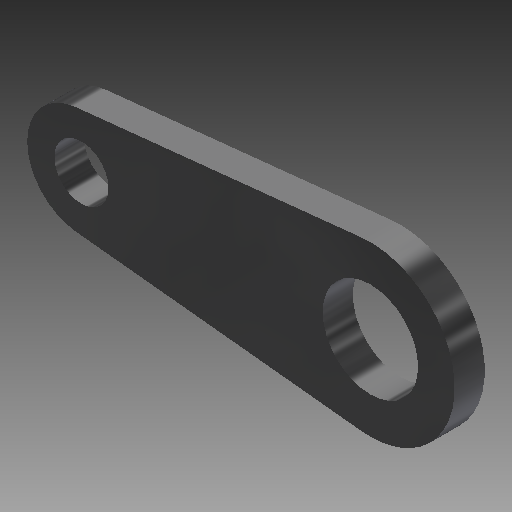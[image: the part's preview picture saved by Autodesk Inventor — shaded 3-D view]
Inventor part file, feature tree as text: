
AUTODESK INVENTOR PART (.ipt)
format: ipt  version: 2019 (Build 230136000, 136)  size: 117,760 bytes
history: native  units: mm
features: sketch x3, hole x2, other x2, extrude x1
ambient origin geometry x8: Origin, YZ Plane, XZ Plane, XY Plane, X Axis, Y Axis, Z Axis, Center Point
bodies: Solid1 (feature_tree)
feature tree (8):
  extrude  "Extrusion1"  Depth=28.0mm
  hole  "Hole1"  [1 undecoded]
  hole  "Hole2"  [1 undecoded]
  other  "Work Point1"
  sketch  "Sketch1"  dims[d0=18.0mm d1=28.0mm]
  sketch  "Sketch2"  dims[d2=48.0mm d3=5.0mm d4=0.0mm]
  sketch  "Sketch3"  dims[d5=15.84mm d6=6.0mm d7=4.0mm d8=2.0mm d9=90.0deg d10=8.0mm d11=20.594885mm d12=9.0mm d13=6.0mm d14=4.0mm d15=2.0mm d16=90.0deg d17=8.0mm d18=20.594885mm]
  other  "Work Axis1"
note: 2 required parameter values undecoded (feature->parameter linkage not recoverable at this tier; creation-order binding heuristic only, values carry confidence <= 0.55)
